# Revit family: Cash-Register
name_source: partatom
category: Specialty Equipment
units: mm (PartAtom-declared; Revit-internal decimal feet)

## family parameters
Always vertical = Yes
Classification Number = 23.40.70.14.37
Cut with Voids When Loaded = No
Enable Cutting in Views = No
Maintain Annotation Orientation = No
Part Type = Normal
Room Calculation Point = No
Round Connector Dimension = Use Diameter
Shared = No
Work Plane-Based = No

## types (1)
- Cash-Register
    Amperage = 2.6
    Assembly Code = E1010520
    Body Material = ARCAT - Plastic, ABS - Tan
    Cash Box Material = ARCAT - Metal - Aluminum, Die Cast
    Cash Drawer = 5 Bill / 5 Slot
    Clerks = 50
    Construction Details = http://www.arcat.com
    Default Elevation = 0' - 0"
    Departments = 99
    Description = Electronic Cash Register
    Display Material = ARCAT - Plastic, Polycarbonate, Grey Clear
    Expected Lifespan (Years) = 0
    Green Building-LEED = http://www.arcat.com
    Interface Ports = RS232 (2)
    Keynote = 11100
    Keypad Material = ARCAT - Plastic, ABS - Grey
    Maintenance Schedule (Months) = 0
    Manufacturer = Generic
    Manufacturer Fax = (203) 939-2444
    Manufacturer Website = http://www.arcat.com
    Model = Generic
    PLUs = 15000
    Printer Type = 2 Station Thermal Printer
    Product Data = http://www.arcat.com
    Product Properties = http://www.arcat.com
    Specification = http://www.arcat.com
    Voltage = 110
    Warranty Duration (Years) = 0
    Wattage = 50

## geometry (parser evidence)
native form markers: Sweep x3
no freeform markers — native parametric forms only
